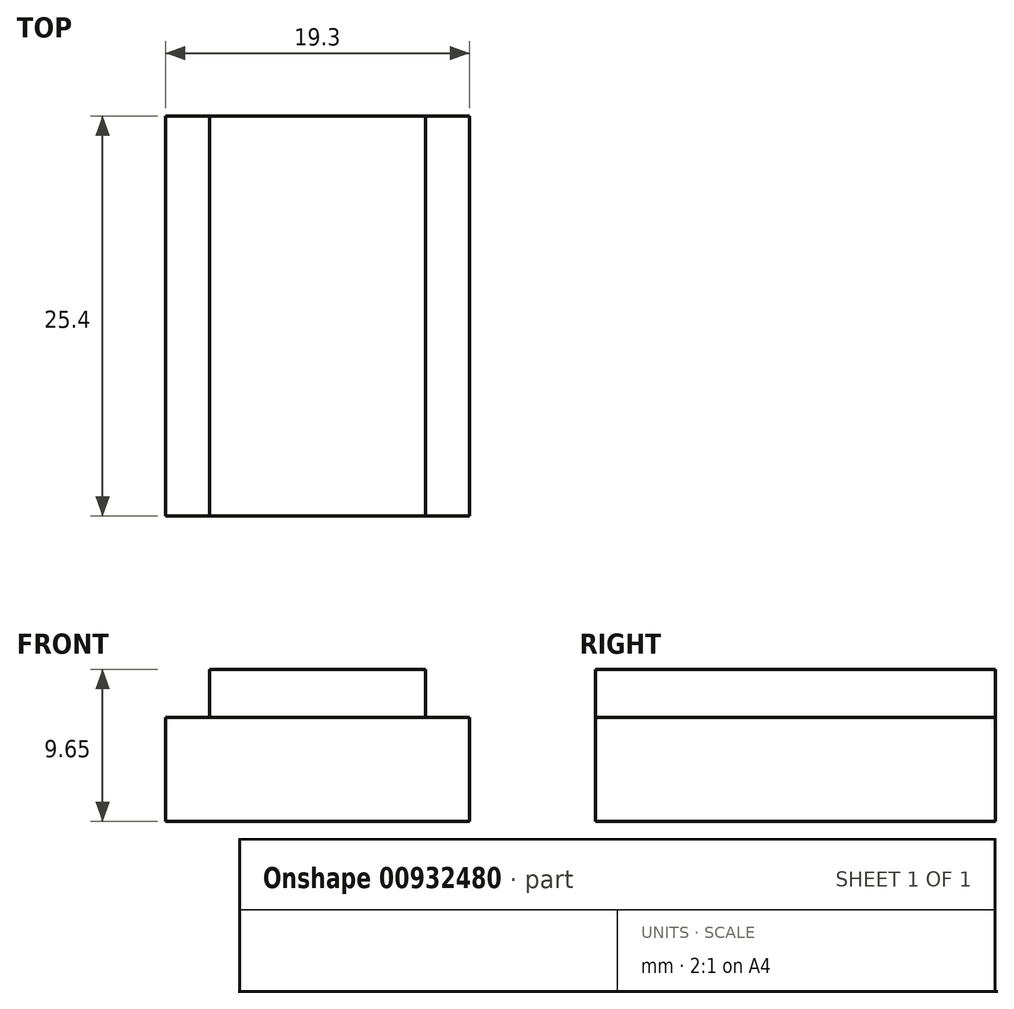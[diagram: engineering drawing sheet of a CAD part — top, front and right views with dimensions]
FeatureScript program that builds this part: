
annotation { "Feature Type Name" : "Feature", "Feature Type Description" : "" }
export const myFeature = defineFeature(function(context is Context, id is Id, definition is map)
    precondition{}
    {
        {
            var Q0;
            Q0=qCreatedBy(makeId("Front.planeOp"),FACE);
            var sketch = newSketch(context, id + "F0", { "sketchPlane" : qUnion([Q0])});
            skLineSegment(sketch, "E0.bottom", {"start": v(9.65, 6.6) * mm, "end": v(-9.65, 6.6) * mm});
            skLineSegment(sketch, "E0.top", {"start": v(9.65, -6.6) * mm, "end": v(-9.65, -6.6) * mm});
            skLineSegment(sketch, "E0.left", {"start": v(9.65, 6.6) * mm, "end": v(9.65, -6.6) * mm});
            skLineSegment(sketch, "E0.right", {"start": v(-9.65, 6.6) * mm, "end": v(-9.65, -6.6) * mm});
            skPoint(sketch, "E0.middle", {"position": v(0, 0) * mm});
            skLineSegment(sketch, "E1", {"start": v(-9.65, 0) * mm, "end": v(9.65, 0) * mm});
            skLineSegment(sketch, "E2", {"start": v(0, 0) * mm, "end": v(0, 3.05) * mm});
            skLineSegment(sketch, "E3", {"start": v(0, 3.05) * mm, "end": v(-6.86, 3.05) * mm});
            skLineSegment(sketch, "E4.bottom", {"start": v(-6.86, 3.05) * mm, "end": v(6.86, 3.05) * mm});
            skLineSegment(sketch, "E4.top", {"start": v(-6.86, -3.05) * mm, "end": v(6.86, -3.05) * mm});
            skLineSegment(sketch, "E4.left", {"start": v(-6.86, 3.05) * mm, "end": v(-6.86, -3.05) * mm});
            skLineSegment(sketch, "E4.right", {"start": v(6.86, 3.05) * mm, "end": v(6.86, -3.05) * mm});
            skLineSegment(sketch, "E5", {"start": v(0, 6.6) * mm, "end": v(8.13, 6.6) * mm});
            skLineSegment(sketch, "E6", {"start": v(0, 6.6) * mm, "end": v(-8.13, 6.6) * mm});
            skSolve(sketch);
        }
        {
            var Q0;
            {var subQ15=sQuery(id+"F0.wireOp",EDGE,"E5");Q0=makeQuery(id+"F0.imprint","IMPRINT",FACE,{"disambiguationData":[TD([[makeQuery(id+"F0.imprint","IMPRINT",EDGE,{"derivedFrom":subQ15}),-1.0]])]});}
            var Q1;
            {var subQ0=sQuery(id+"F0.wireOp",EDGE,"E2");Q1=makeQuery(id+"F0.imprint","IMPRINT",FACE,{"disambiguationData":[TD([[makeQuery(id+"F0.imprint","IMPRINT",EDGE,{"derivedFrom":subQ0}),1.0]])]});}
            var Q2;
            {var subQ0=sQuery(id+"F0.wireOp",EDGE,"E2");Q2=makeQuery(id+"F0.imprint","IMPRINT",FACE,{"disambiguationData":[TD([[makeQuery(id+"F0.imprint","IMPRINT",EDGE,{"derivedFrom":subQ0}),-1.0]])]});}
            extrude(context, id + "F1", {"entities" : qUnion([Q0, Q1, Q2]), "oppositeDirection" : true, "depth" : 25.4 * mm, "offsetDistance" : 25.4 * mm});
        }
        {
            var Q0;
            {var subQ1=sQuery(id+"F0.wireOp",EDGE,"E0.top");Q0=makeQuery(id+"F0.imprint","IMPRINT",FACE,{"disambiguationData":[TD([[makeQuery(id+"F0.imprint","IMPRINT",EDGE,{"derivedFrom":subQ1}),-1.0]])]});}
            var Q1;
            {var subQ1=sQuery(id+"F0.wireOp",EDGE,"E4.top");Q1=makeQuery(id+"F0.imprint","IMPRINT",FACE,{"disambiguationData":[TD([[makeQuery(id+"F0.imprint","IMPRINT",EDGE,{"derivedFrom":subQ1}),1.0]])]});}
            extrude(context, id + "F2", {"entities" : qUnion([Q0, Q1]), "oppositeDirection" : true, "depth" : 25.4 * mm, "offsetDistance" : 25.4 * mm});
        }
    });
